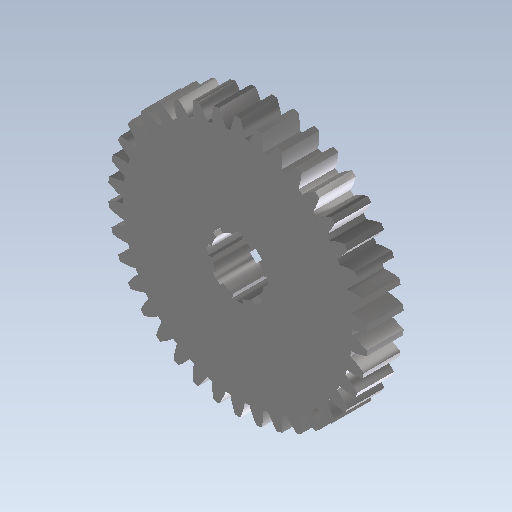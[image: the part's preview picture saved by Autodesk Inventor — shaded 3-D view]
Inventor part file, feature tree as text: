
AUTODESK INVENTOR PART (.ipt)
format: ipt  version: 2020 (Build 240168000, 168)  size: 354,304 bytes
history: native  units: mm (DEFAULTED — no unit token found)
features: extrude x3, plane x3, other x3, sketch x2, pattern_circular x1
ambient origin geometry x8: Origin, YZ Plane, XZ Plane, XY Plane, X Axis, Y Axis, Z Axis, Center Point
bodies: Solid1 (feature_tree)
feature tree (12):
  extrude  "Extrusion1"  Depth=1.4mm TaperAngle=0.0deg
  plane  "Work Plane2"
  plane  "Work Plane8"
  plane  "Work Plane9"
  other  "Цилиндрическое зубчатое зацепление"
  sketch  "Эскиз3"
  extrude  "Выдавливание2"  Depth=10.0mm
  extrude  "Выдавливание3"  Depth=10.0mm TaperAngle=0.0deg
  pattern_circular  "Круговой массив1"  [2 undecoded]
  sketch  "Sketch2"  dims[d0=9.865mm d1=1.4mm d2=0.0mm d3=9.5mm d4=10.0mm d5=0.0mm d16=6.0mm d17=0.0mm d34=0.826735mm d39=0.0mm d41=0.0mm d43=6.0mm d46=6.0mm d47=0.0mm d48=0.0mm d49=2.0mm d50=0.15mm d51=3.490659mm d52=10.0mm d53=0.0mm d54=10.0mm d55=0.0mm d56=80.0mm d57=360.0deg]
  other  "Srf1"
  other  "Средний диаметр"
note: 2 required parameter values undecoded (feature->parameter linkage not recoverable at this tier; creation-order binding heuristic only, values carry confidence <= 0.55)
